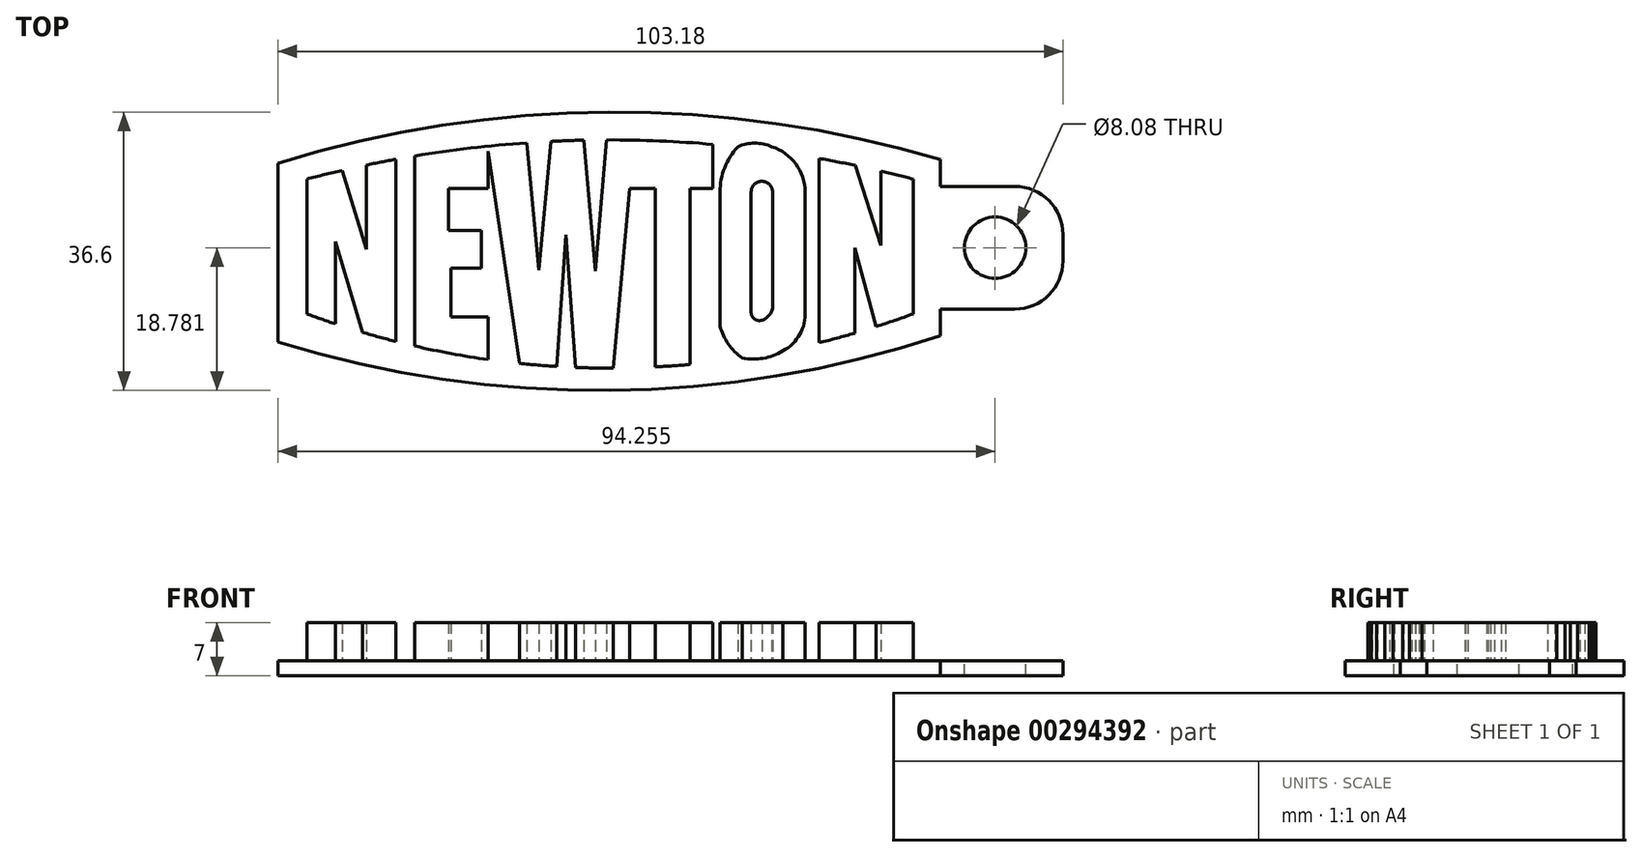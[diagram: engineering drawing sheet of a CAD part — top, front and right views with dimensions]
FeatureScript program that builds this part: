
annotation { "Feature Type Name" : "Feature", "Feature Type Description" : "" }
export const myFeature = defineFeature(function(context is Context, id is Id, definition is map)
    precondition{}
    {
        {
            var Q0;
            Q0=qCreatedBy(makeId("Top.planeOp"),FACE);
            var sketch = newSketch(context, id + "F0", { "sketchPlane" : qUnion([Q0])});
            skLineSegment(sketch, "E0", {"start": v(-31.31, 16.26) * mm, "end": v(-31.31, -1.45) * mm});
            skArc(sketch, "E1", {"start": v(48.39, 16.26) * mm, "mid": v(46.26, 16.8) * mm, "end": v(44.12, 17.32) * mm});
            skArc(sketch, "E2", {"start": v(-31.31, -1.45) * mm, "mid": v(-29.45, -2.13) * mm, "end": v(-27.57, -2.77) * mm});
            skLineSegment(sketch, "E3", {"start": v(48.39, 16.26) * mm, "end": v(48.39, -1.45) * mm});
            skLineSegment(sketch, "E4", {"start": v(-27.57, -2.77) * mm, "end": v(-27.57, 8.04) * mm});
            skLineSegment(sketch, "E5", {"start": v(-27.57, 8.04) * mm, "end": v(-23.98, -3.9) * mm});
            skLineSegment(sketch, "E6", {"start": v(-19.58, -5.1) * mm, "end": v(-19.58, 18.87) * mm});
            skLineSegment(sketch, "E7", {"start": v(-23.49, 18.1) * mm, "end": v(-23.49, 7.05) * mm});
            skLineSegment(sketch, "E8", {"start": v(-23.49, 7.05) * mm, "end": v(-26.65, 17.4) * mm});
            skArc(sketch, "E9.trimOffspring", {"start": v(-26.65, 17.4) * mm, "mid": v(-28.99, 16.85) * mm, "end": v(-31.31, 16.26) * mm});
            skArc(sketch, "E10.trimOffspring", {"start": v(-23.98, -3.9) * mm, "mid": v(-21.79, -4.52) * mm, "end": v(-19.58, -5.1) * mm});
            skLineSegment(sketch, "E11", {"start": v(-17.12, 19.3) * mm, "end": v(-17.12, -5.69) * mm});
            skLineSegment(sketch, "E12", {"start": v(-7.46, 20.6) * mm, "end": v(-7.46, 15.06) * mm});
            skLineSegment(sketch, "E13", {"start": v(-7.46, 15.06) * mm, "end": v(-12.69, 15.06) * mm});
            skLineSegment(sketch, "E14", {"start": v(-12.69, 15.06) * mm, "end": v(-12.69, 9.52) * mm});
            skLineSegment(sketch, "E15", {"start": v(-12.69, 9.52) * mm, "end": v(-8.33, 9.52) * mm});
            skLineSegment(sketch, "E16", {"start": v(-8.33, 9.52) * mm, "end": v(-8.33, 4.58) * mm});
            skLineSegment(sketch, "E17", {"start": v(-8.33, 4.58) * mm, "end": v(-12.39, 4.58) * mm});
            skLineSegment(sketch, "E18", {"start": v(-12.39, 4.58) * mm, "end": v(-12.39, -1.85) * mm});
            skLineSegment(sketch, "E19", {"start": v(-12.39, -1.85) * mm, "end": v(-7.46, -1.85) * mm});
            skLineSegment(sketch, "E20", {"start": v(-7.46, -1.85) * mm, "end": v(-7.46, -7.47) * mm});
            skArc(sketch, "E21.trimOffspring", {"start": v(-19.58, 18.87) * mm, "mid": v(-21.54, 18.5) * mm, "end": v(-23.49, 18.1) * mm});
            skArc(sketch, "E22.trimOffspring", {"start": v(-17.12, -5.69) * mm, "mid": v(-12.3, -6.68) * mm, "end": v(-7.46, -7.47) * mm});
            skLineSegment(sketch, "E23", {"start": v(-7.55, 20.58) * mm, "end": v(-3.32, -7.98) * mm});
            skLineSegment(sketch, "E24", {"start": v(-2.41, 21.03) * mm, "end": v(-0.82, 4.28) * mm});
            skLineSegment(sketch, "E25", {"start": v(-0.82, 4.28) * mm, "end": v(0.75, 21.22) * mm});
            skLineSegment(sketch, "E26", {"start": v(5.12, 21.37) * mm, "end": v(6.6, 4.18) * mm});
            skLineSegment(sketch, "E27", {"start": v(6.6, 4.18) * mm, "end": v(8.1, 21.41) * mm});
            skLineSegment(sketch, "E28", {"start": v(1.53, -8.38) * mm, "end": v(2.75, 8.93) * mm});
            skLineSegment(sketch, "E29", {"start": v(2.75, 8.93) * mm, "end": v(4.03, -8.5) * mm});
            skLineSegment(sketch, "E30", {"start": v(8.98, -8.6) * mm, "end": v(11.16, 15.06) * mm});
            skLineSegment(sketch, "E31", {"start": v(11.16, 15.06) * mm, "end": v(14.53, 15.06) * mm});
            skLineSegment(sketch, "E32", {"start": v(14.53, 15.06) * mm, "end": v(14.53, -8.44) * mm});
            skLineSegment(sketch, "E33", {"start": v(22.04, 20.83) * mm, "end": v(22.04, 15.06) * mm});
            skLineSegment(sketch, "E34", {"start": v(22.04, 15.06) * mm, "end": v(19.08, 15.06) * mm});
            skLineSegment(sketch, "E35", {"start": v(19.08, 15.06) * mm, "end": v(19.08, -8.1) * mm});
            skLineSegment(sketch, "E36", {"start": v(36.04, -5.25) * mm, "end": v(36.04, 18.98) * mm});
            skLineSegment(sketch, "E37", {"start": v(40.77, 18.06) * mm, "end": v(44.12, 7.54) * mm});
            skLineSegment(sketch, "E38", {"start": v(44.12, 7.54) * mm, "end": v(44.12, 17.32) * mm});
            skLineSegment(sketch, "E39", {"start": v(40.7, -4) * mm, "end": v(40.7, 7.25) * mm});
            skLineSegment(sketch, "E40", {"start": v(40.7, 7.25) * mm, "end": v(43.52, -3.13) * mm});
            skArc(sketch, "E41.trimOffspring", {"start": v(40.77, 18.06) * mm, "mid": v(38.4, 18.54) * mm, "end": v(36.04, 18.98) * mm});
            skArc(sketch, "E42.trimOffspring", {"start": v(43.52, -3.13) * mm, "mid": v(45.97, -2.32) * mm, "end": v(48.39, -1.45) * mm});
            skArc(sketch, "E43.trimOffspring", {"start": v(5.12, 21.37) * mm, "mid": v(2.94, 21.31) * mm, "end": v(0.75, 21.22) * mm});
            skArc(sketch, "E44.trimOffspring", {"start": v(-2.41, 21.03) * mm, "mid": v(-9.78, 20.34) * mm, "end": v(-17.12, 19.3) * mm});
            skArc(sketch, "E45.trimOffspring", {"start": v(4.03, -8.5) * mm, "mid": v(6.5, -8.57) * mm, "end": v(8.98, -8.6) * mm});
            skArc(sketch, "E46.trimOffspring", {"start": v(-3.32, -7.98) * mm, "mid": v(-0.9, -8.2) * mm, "end": v(1.53, -8.38) * mm});
            skArc(sketch, "E47.trimOffspring", {"start": v(14.53, -8.44) * mm, "mid": v(16.8, -8.3) * mm, "end": v(19.08, -8.1) * mm});
            skLineSegment(sketch, "E48", {"start": v(23.01, 14.56) * mm, "end": v(23.01, -3.04) * mm});
            skLineSegment(sketch, "E49", {"start": v(27.1, 14.56) * mm, "end": v(27.1, -1.27) * mm});
            skLineSegment(sketch, "E50", {"start": v(29.92, 14.56) * mm, "end": v(29.92, 0) * mm});
            skLineSegment(sketch, "E51", {"start": v(34.18, 14.56) * mm, "end": v(34.18, -1.12) * mm});
            skArc(sketch, "E52", {"start": v(25.34, 20.5) * mm, "mid": v(23.61, 17.76) * mm, "end": v(23.01, 14.56) * mm});
            skArc(sketch, "E53", {"start": v(29.82, 20.5) * mm, "mid": v(27.58, 20.98) * mm, "end": v(25.34, 20.5) * mm});
            skArc(sketch, "E54", {"start": v(34.18, 14.56) * mm, "mid": v(32.97, 18.25) * mm, "end": v(29.82, 20.5) * mm});
            skArc(sketch, "E55.trimOffspring", {"start": v(22.04, 20.83) * mm, "mid": v(15.08, 21.28) * mm, "end": v(8.1, 21.41) * mm});
            skArc(sketch, "E56", {"start": v(29.92, 14.56) * mm, "mid": v(28.5, 15.98) * mm, "end": v(27.1, 14.56) * mm});
            skArc(sketch, "E57", {"start": v(27.1, -1.27) * mm, "mid": v(27.54, -2.14) * mm, "end": v(28.51, -2.3) * mm});
            skArc(sketch, "E58", {"start": v(23.01, -3.04) * mm, "mid": v(24.1, -5.41) * mm, "end": v(25.92, -7.27) * mm});
            skArc(sketch, "E59", {"start": v(25.92, -7.27) * mm, "mid": v(28.68, -7.3) * mm, "end": v(31.25, -6.32) * mm});
            skArc(sketch, "E60", {"start": v(31.25, -6.32) * mm, "mid": v(33.5, -4.16) * mm, "end": v(34.18, -1.12) * mm});
            skArc(sketch, "E61.trimOffspring", {"start": v(36.04, -5.25) * mm, "mid": v(38.37, -4.65) * mm, "end": v(40.7, -4) * mm});
            skArc(sketch, "E62", {"start": v(28.51, -2.3) * mm, "mid": v(29.65, -1.41) * mm, "end": v(29.92, 0) * mm});
            skSolve(sketch);
        }
        {
            var Q0;
            Q0 = qSketchRegion(id + "F0", true);
            extrude(context, id + "F1", {"entities" : qUnion([Q0]), "depth" : 5 * mm});
        }
        {
            var Q0;
            Q0=qCreatedBy(makeId("Top.planeOp"),FACE);
            var sketch = newSketch(context, id + "F2", { "sketchPlane" : qUnion([Q0])});
            skLineSegment(sketch, "E63", {"start": v(-35.09, 18.36) * mm, "end": v(-35.09, -5.17) * mm});
            skLineSegment(sketch, "E64", {"start": v(51.96, 18.83) * mm, "end": v(51.96, -4.34) * mm});
            skArc(sketch, "E65", {"start": v(51.96, 18.83) * mm, "mid": v(8.4, 25.06) * mm, "end": v(-35.09, 18.36) * mm});
            skArc(sketch, "E66", {"start": v(-35.09, -5.17) * mm, "mid": v(8.5, -11.53) * mm, "end": v(51.96, -4.34) * mm});
            skSolve(sketch);
        }
        {
            var Q0;
            Q0 = qSketchRegion(id + "F2", true);
            extrude(context, id + "F3", {"entities" : qUnion([Q0]), "oppositeDirection" : true, "depth" : 2 * mm});
        }
        {
            var Q0;
            Q0=makeQuery(id+"F1.opExtrude","SWEPT_BODY",BODY,{"disambiguationData":[OSD([sQuery(id+"F0.wireOp",EDGE,"E0"),sQuery(id+"F0.wireOp",EDGE,"E2"),sQuery(id+"F0.wireOp",EDGE,"E4"),sQuery(id+"F0.wireOp",EDGE,"E5"),sQuery(id+"F0.wireOp",EDGE,"E6"),sQuery(id+"F0.wireOp",EDGE,"E7"),sQuery(id+"F0.wireOp",EDGE,"E8"),sQuery(id+"F0.wireOp",EDGE,"E9.trimOffspring"),sQuery(id+"F0.wireOp",EDGE,"E10.trimOffspring"),sQuery(id+"F0.wireOp",EDGE,"E21.trimOffspring")])]});
            var Q1;
            Q1=makeQuery(id+"F1.opExtrude","SWEPT_BODY",BODY,{"disambiguationData":[OSD([sQuery(id+"F0.wireOp",EDGE,"E1"),sQuery(id+"F0.wireOp",EDGE,"E3"),sQuery(id+"F0.wireOp",EDGE,"E36"),sQuery(id+"F0.wireOp",EDGE,"E37"),sQuery(id+"F0.wireOp",EDGE,"E38"),sQuery(id+"F0.wireOp",EDGE,"E39"),sQuery(id+"F0.wireOp",EDGE,"E40"),sQuery(id+"F0.wireOp",EDGE,"E41.trimOffspring"),sQuery(id+"F0.wireOp",EDGE,"E42.trimOffspring"),sQuery(id+"F0.wireOp",EDGE,"E61.trimOffspring")])]});
            var Q2;
            Q2=makeQuery(id+"F1.opExtrude","SWEPT_BODY",BODY,{"disambiguationData":[OSD([sQuery(id+"F0.wireOp",EDGE,"E11"),sQuery(id+"F0.wireOp",EDGE,"E12"),sQuery(id+"F0.wireOp",EDGE,"E13"),sQuery(id+"F0.wireOp",EDGE,"E14"),sQuery(id+"F0.wireOp",EDGE,"E15"),sQuery(id+"F0.wireOp",EDGE,"E16"),sQuery(id+"F0.wireOp",EDGE,"E17"),sQuery(id+"F0.wireOp",EDGE,"E18"),sQuery(id+"F0.wireOp",EDGE,"E19"),sQuery(id+"F0.wireOp",EDGE,"E20"),sQuery(id+"F0.wireOp",EDGE,"E22.trimOffspring"),sQuery(id+"F0.wireOp",EDGE,"E23"),sQuery(id+"F0.wireOp",EDGE,"E24"),sQuery(id+"F0.wireOp",EDGE,"E25"),sQuery(id+"F0.wireOp",EDGE,"E26"),sQuery(id+"F0.wireOp",EDGE,"E27"),sQuery(id+"F0.wireOp",EDGE,"E28"),sQuery(id+"F0.wireOp",EDGE,"E29"),sQuery(id+"F0.wireOp",EDGE,"E30"),sQuery(id+"F0.wireOp",EDGE,"E31"),sQuery(id+"F0.wireOp",EDGE,"E32"),sQuery(id+"F0.wireOp",EDGE,"E33"),sQuery(id+"F0.wireOp",EDGE,"E34"),sQuery(id+"F0.wireOp",EDGE,"E35"),sQuery(id+"F0.wireOp",EDGE,"E43.trimOffspring"),sQuery(id+"F0.wireOp",EDGE,"E44.trimOffspring"),sQuery(id+"F0.wireOp",EDGE,"E45.trimOffspring"),sQuery(id+"F0.wireOp",EDGE,"E46.trimOffspring"),sQuery(id+"F0.wireOp",EDGE,"E47.trimOffspring"),sQuery(id+"F0.wireOp",EDGE,"E55.trimOffspring")])]});
            var Q3;
            Q3=makeQuery(id+"F1.opExtrude","SWEPT_BODY",BODY,{"disambiguationData":[OSD([sQuery(id+"F0.wireOp",EDGE,"E48"),sQuery(id+"F0.wireOp",EDGE,"E49"),sQuery(id+"F0.wireOp",EDGE,"E50"),sQuery(id+"F0.wireOp",EDGE,"E51"),sQuery(id+"F0.wireOp",EDGE,"E52"),sQuery(id+"F0.wireOp",EDGE,"E53"),sQuery(id+"F0.wireOp",EDGE,"E54"),sQuery(id+"F0.wireOp",EDGE,"E56"),sQuery(id+"F0.wireOp",EDGE,"E57"),sQuery(id+"F0.wireOp",EDGE,"E58"),sQuery(id+"F0.wireOp",EDGE,"E59"),sQuery(id+"F0.wireOp",EDGE,"E60"),sQuery(id+"F0.wireOp",EDGE,"E62")])]});
            var Q4;
            Q4=makeQuery(id+"F3.opExtrude","SWEPT_BODY",BODY,{"disambiguationData":[OSD([sQuery(id+"F2.wireOp",EDGE,"E63"),sQuery(id+"F2.wireOp",EDGE,"E64"),sQuery(id+"F2.wireOp",EDGE,"E65"),sQuery(id+"F2.wireOp",EDGE,"E66")])]});
            booleanBodies(context, id + "F4", {"operationType" : BooleanOperationType.UNION, "tools" : qUnion([Q0, Q1, Q2, Q3, Q4])});
        }
        {
            var Q0;
            {var subQ0=sQuery(id+"F2.wireOp",EDGE,"E66");var subQ1=sQuery(id+"F2.wireOp",EDGE,"E63");var subQ2=sQuery(id+"F2.wireOp",EDGE,"E64");var subQ3=sQuery(id+"F2.wireOp",EDGE,"E65");Q0=makeQuery(id+"F4.opBoolean","SPLIT",FACE,{"disambiguationData":[TD([makeQuery(id+"F1.opExtrude","SWEPT_FACE",FACE,{"disambiguationData":[OSD([sQuery(id+"F0.wireOp",EDGE,"E0")])]})])],"derivedFrom":makeQuery(id+"F3.opExtrude","CAP_FACE",FACE,{"disambiguationData":[OSD([subQ1,subQ2,subQ3,subQ0])],"isStart":true})});}
            var sketch = newSketch(context, id + "F5", { "sketchPlane" : qUnion([Q0])});
            skPoint(sketch, "E67.centerSnap0", {"position": v(51.96, 7.24) * mm});
            skLineSegment(sketch, "E68", {"start": v(51.96, 7.24) * mm, "end": v(51.96, 15.3) * mm});
            skLineSegment(sketch, "E69", {"start": v(51.96, 15.3) * mm, "end": v(61.74, 15.3) * mm});
            skLineSegment(sketch, "E70", {"start": v(68.09, 8.96) * mm, "end": v(68.09, 5.53) * mm});
            skLineSegment(sketch, "E71", {"start": v(61.74, -0.82) * mm, "end": v(51.96, -0.82) * mm});
            skLineSegment(sketch, "E72", {"start": v(51.96, -0.82) * mm, "end": v(51.96, 7.24) * mm});
            skPoint(sketch, "E73.visualSharp", {"position": v(68.09, 15.3) * mm});
            skArc(sketch, "E73.filletArc", {"start": v(68.09, 8.96) * mm, "mid": v(66.23, 13.45) * mm, "end": v(61.74, 15.3) * mm});
            skPoint(sketch, "E74.visualSharp", {"position": v(68.09, -0.82) * mm});
            skArc(sketch, "E74.filletArc", {"start": v(61.74, -0.82) * mm, "mid": v(66.23, 1.04) * mm, "end": v(68.09, 5.53) * mm});
            skCircle(sketch, "E75", {"center": v(59.17, 7.24) * mm, "radius": 4.04 * mm});
            skPoint(sketch, "E75.centerSnap0", {"position": v(68.09, 7.24) * mm});
            skSolve(sketch);
        }
        {
            var Q0;
            Q0 = qSketchRegion(id + "F5", true);
            extrude(context, id + "F6", {"entities" : qUnion([Q0]), "operationType" : NewBodyOperationType.ADD, "oppositeDirection" : true, "depth" : 2 * mm});
        }
    });
